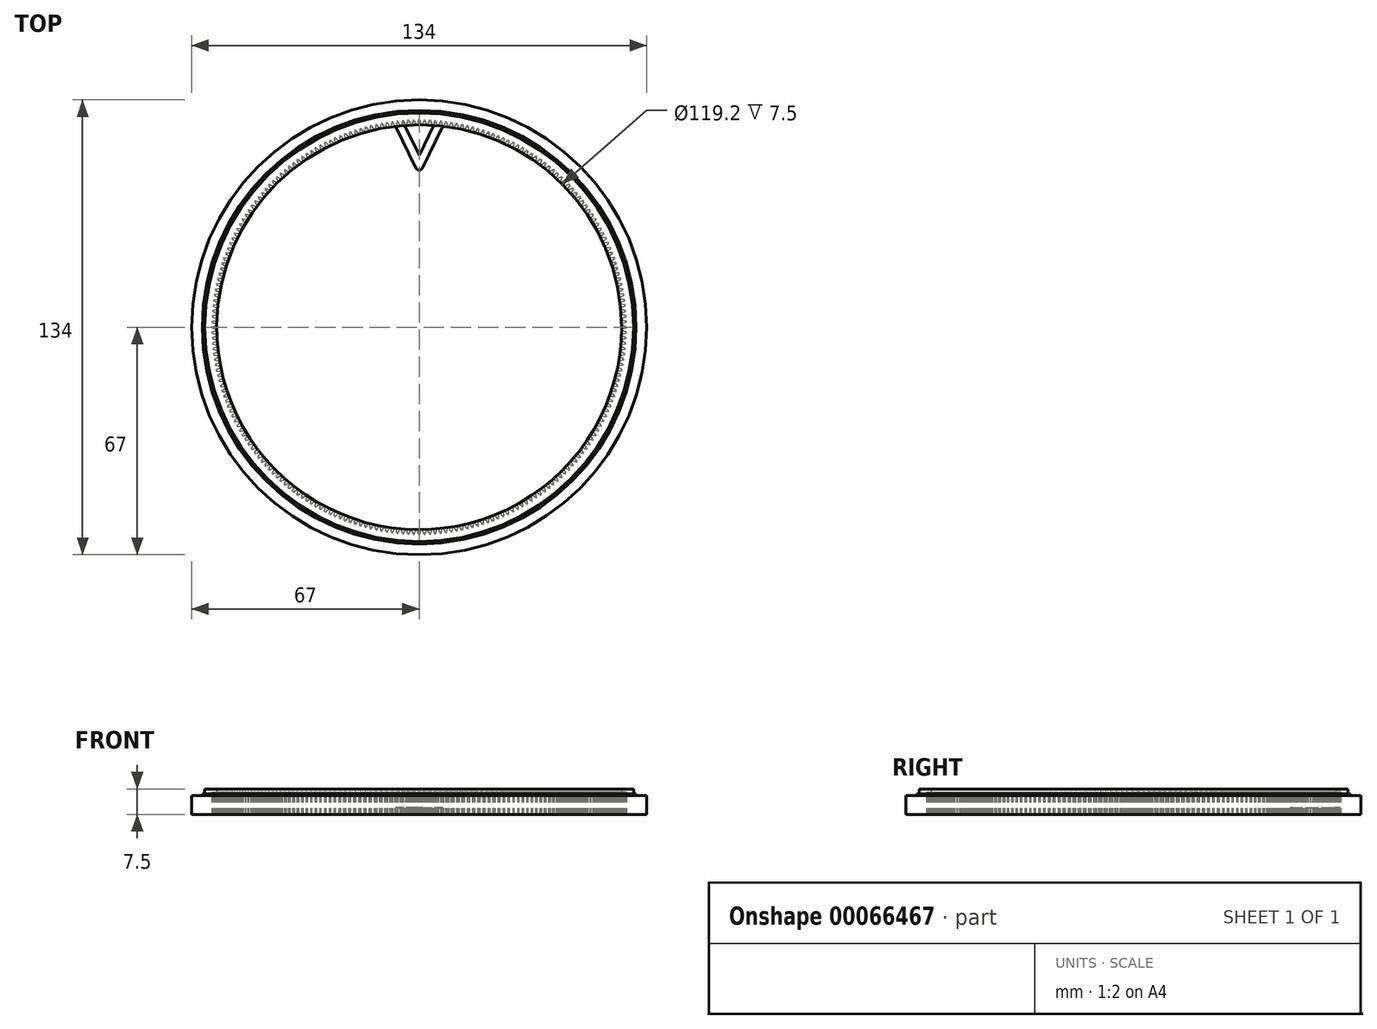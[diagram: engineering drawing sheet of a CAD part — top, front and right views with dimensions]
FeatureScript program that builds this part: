
annotation { "Feature Type Name" : "Feature", "Feature Type Description" : "" }
export const myFeature = defineFeature(function(context is Context, id is Id, definition is map)
    precondition{}
    {
        {
            var Q0;
            Q0=qCreatedBy(makeId("Top.planeOp"),FACE);
            var sketch = newSketch(context, id + "F0", { "sketchPlane" : qUnion([Q0])});
            skCircle(sketch, "E0", {"center": v(0, 0) * mm, "radius": 59.6 * mm});
            skCircle(sketch, "E1", {"center": v(0, 0) * mm, "radius": 67 * mm});
            skSolve(sketch);
        }
        {
            var Q0;
            Q0=makeQuery(id+"F0.imprint","IMPRINT",FACE,{"disambiguationData":[TD([[makeQuery(id+"F0.imprint","IMPRINT",EDGE,{"derivedFrom":sQuery(id+"F0.wireOp",EDGE,"E0")}),-1.0]])]});
            extrude(context, id + "F1", {"entities" : qUnion([Q0]), "endBound" : BoundingType.SYMMETRIC, "depth" : 7.5 * mm});
        }
        {
            var Q0;
            Q0=makeQuery(id+"F1.opExtrude","CAP_FACE",FACE,{"disambiguationData":[OSD([sQuery(id+"F0.wireOp",EDGE,"E0"),sQuery(id+"F0.wireOp",EDGE,"E1")])],"isStart":false});
            var sketch = newSketch(context, id + "F2", { "sketchPlane" : qUnion([Q0])});
            skCircle(sketch, "E2", {"center": v(0, 0) * mm, "radius": 63.12 * mm});
            skCircle(sketch, "E3", {"center": v(0, 0) * mm, "radius": 63.88 * mm});
            skSolve(sketch);
        }
        {
            var Q0;
            Q0=makeQuery(id+"F2.imprint","IMPRINT",FACE,{"disambiguationData":[TD([[makeQuery(id+"F2.imprint","IMPRINT",EDGE,{"derivedFrom":sQuery(id+"F2.wireOp",EDGE,"E2")}),-1.0]])]});
            extrude(context, id + "F3", {"entities" : qUnion([Q0]), "operationType" : NewBodyOperationType.REMOVE, "oppositeDirection" : true, "depth" : 1.5 * mm});
        }
        {
            var Q0;
            {var subQ0=sQuery(id+"F0.wireOp",EDGE,"E1");Q0=makeQuery(id+"F3.boolean.opBoolean","SPLIT",FACE,{"disambiguationData":[TD([makeQuery(id+"F1.opExtrude","SWEPT_FACE",FACE,{"disambiguationData":[OSD([subQ0])]})])],"derivedFrom":makeQuery(id+"F1.opExtrude","CAP_FACE",FACE,{"disambiguationData":[OSD([sQuery(id+"F0.wireOp",EDGE,"E0"),subQ0])],"isStart":false})});}
            extrude(context, id + "F4", {"entities" : qUnion([Q0]), "operationType" : NewBodyOperationType.REMOVE, "oppositeDirection" : true, "depth" : 2 * mm});
        }
        {
            var Q0;
            Q0=makeQuery(id+"F1.opExtrude","CAP_FACE",FACE,{"disambiguationData":[OSD([sQuery(id+"F0.wireOp",EDGE,"E0"),sQuery(id+"F0.wireOp",EDGE,"E1")])],"isStart":true});
            var sketch = newSketch(context, id + "F5", { "sketchPlane" : qUnion([Q0])});
            skCircle(sketch, "E4", {"center": v(0, 0) * mm, "radius": 61 * mm, "construction": true});
            skLineSegment(sketch, "E5", {"start": v(0, 0) * mm, "end": v(-61, 0) * mm, "construction": true});
            skLineSegment(sketch, "E6", {"start": v(-61, -0.15) * mm, "end": v(-61, 0.15) * mm});
            skPoint(sketch, "E7", {"position": v(-59.4, 0) * mm});
            skLineSegment(sketch, "E8", {"start": v(-59.4, -0.67) * mm, "end": v(-59.4, 0.67) * mm});
            skLineSegment(sketch, "E9", {"start": v(-61, -0.15) * mm, "end": v(-59.4, -0.68) * mm});
            skLineSegment(sketch, "E10", {"start": v(-61, 0.15) * mm, "end": v(-59.4, 0.68) * mm});
            skSolve(sketch);
        }
        {
            var Q0;
            {var subQ0=sQuery(id+"F5.wireOp",EDGE,"E6");Q0=makeQuery(id+"F5.imprint","IMPRINT",FACE,{"disambiguationData":[TD([[makeQuery(id+"F5.imprint","IMPRINT",EDGE,{"derivedFrom":subQ0}),-1.0]])]});}
            var Q1;
            {var subQ0=sQuery(id+"F5.wireOp",EDGE,"E8");Q1=makeQuery(id+"F5.imprint","IMPRINT",FACE,{"disambiguationData":[TD([[makeQuery(id+"F5.imprint","IMPRINT",EDGE,{"derivedFrom":subQ0}),1.0]])]});}
            extrude(context, id + "F6", {"entities" : qUnion([Q0, Q1]), "operationType" : NewBodyOperationType.REMOVE, "oppositeDirection" : true, "depth" : 6.5 * mm});
        }
        {
            var Q0;
            Q0=makeQuery(id+"F6.boolean.opBoolean","COPY",FACE,{"derivedFrom":makeQuery(id+"F6.opExtrude","CAP_FACE",FACE,{"disambiguationData":[OSD([sQuery(id+"F5.wireOp",EDGE,"E6"),sQuery(id+"F5.wireOp",EDGE,"E8"),sQuery(id+"F5.wireOp",EDGE,"E9"),sQuery(id+"F5.wireOp",EDGE,"E10")])],"isStart":false})});
            var Q1;
            Q1=makeQuery(id+"F6.boolean.opBoolean","COPY",FACE,{"derivedFrom":makeQuery(id+"F6.opExtrude","SWEPT_FACE",FACE,{"disambiguationData":[OSD([sQuery(id+"F5.wireOp",EDGE,"E9")])]})});
            var Q2;
            Q2=makeQuery(id+"F6.boolean.opBoolean","COPY",FACE,{"derivedFrom":makeQuery(id+"F6.opExtrude","SWEPT_FACE",FACE,{"disambiguationData":[OSD([sQuery(id+"F5.wireOp",EDGE,"E6")])]})});
            var Q3;
            Q3=makeQuery(id+"F6.boolean.opBoolean","COPY",FACE,{"derivedFrom":makeQuery(id+"F6.opExtrude","SWEPT_FACE",FACE,{"disambiguationData":[OSD([sQuery(id+"F5.wireOp",EDGE,"E10")])]})});
            var Q4;
            Q4=makeQuery(id+"F1.opExtrude","CAP_EDGE",EDGE,{"disambiguationData":[OSD([sQuery(id+"F0.wireOp",EDGE,"E1")])],"isStart":true});
            circularPattern(context, id + "F7", {"faces" : qUnion([Q0, Q1, Q2, Q3]), "axis" : qUnion([Q4]), "angle" : 360 * degree, "instanceCount" : 240, "equalSpace" : true, "patternType" : PatternType.FACE});
        }
        {
            var Q0;
            Q0=makeQuery(id+"F1.opExtrude","CAP_FACE",FACE,{"disambiguationData":[OSD([sQuery(id+"F0.wireOp",EDGE,"E0"),sQuery(id+"F0.wireOp",EDGE,"E1")])],"isStart":true});
            var sketch = newSketch(context, id + "F8", { "sketchPlane" : qUnion([Q0])});
            skCircle(sketch, "E11.0", {"center": v(0, 0) * mm, "radius": 63.12 * mm, "construction": true});
            skLineSegment(sketch, "E12", {"start": v(0, 0) * mm, "end": v(0, -45) * mm, "construction": true});
            skLineSegment(sketch, "E13", {"start": v(0, 0) * mm, "end": v(-10.75, -76.49) * mm, "construction": true});
            skLineSegment(sketch, "E14", {"start": v(0, -63.12) * mm, "end": v(-8.87, -63.12) * mm});
            skLineSegment(sketch, "E15", {"start": v(0, -45) * mm, "end": v(-8.87, -63.12) * mm});
            skLineSegment(sketch, "E16.MirrorCS", {"start": v(0, -63.12) * mm, "end": v(8.87, -63.12) * mm});
            skLineSegment(sketch, "E17.MirrorCS", {"start": v(0, -45) * mm, "end": v(8.87, -63.12) * mm});
            skLineSegment(sketch, "E18.0", {"start": v(0, -50.69) * mm, "end": v(4.86, -60.63) * mm});
            skLineSegment(sketch, "E18.1", {"start": v(0, -50.69) * mm, "end": v(-4.86, -60.63) * mm});
            skLineSegment(sketch, "E18.2", {"start": v(0, -60.63) * mm, "end": v(-4.86, -60.63) * mm});
            skLineSegment(sketch, "E18.3", {"start": v(0, -60.62) * mm, "end": v(4.86, -60.62) * mm});
            skSolve(sketch);
        }
        {
            var Q0;
            {var subQ7=sQuery(id+"F8.wireOp",EDGE,"E18.0");Q0=makeQuery(id+"F8.imprint","IMPRINT",FACE,{"disambiguationData":[TD([[makeQuery(id+"F8.imprint","IMPRINT",EDGE,{"derivedFrom":subQ7}),1.0]])]});}
            extrude(context, id + "F9", {"entities" : qUnion([Q0]), "operationType" : NewBodyOperationType.ADD, "oppositeDirection" : true, "depth" : 2 * mm});
        }
        {
            var Q0;
            Q0=makeQuery(id+"F9.opExtrude","SWEPT_EDGE",EDGE,{"disambiguationData":[OSD([sQuery(id+"F8.wireOp",EDGE,"E15"),sQuery(id+"F8.wireOp",EDGE,"E17.MirrorCS")])]});
            fillet(context, id + "F10", {"entities" : qUnion([Q0]), "radius" : 1 * mm, "tangentPropagation" : true, "allowEdgeOverflow" : false});
        }
    });
